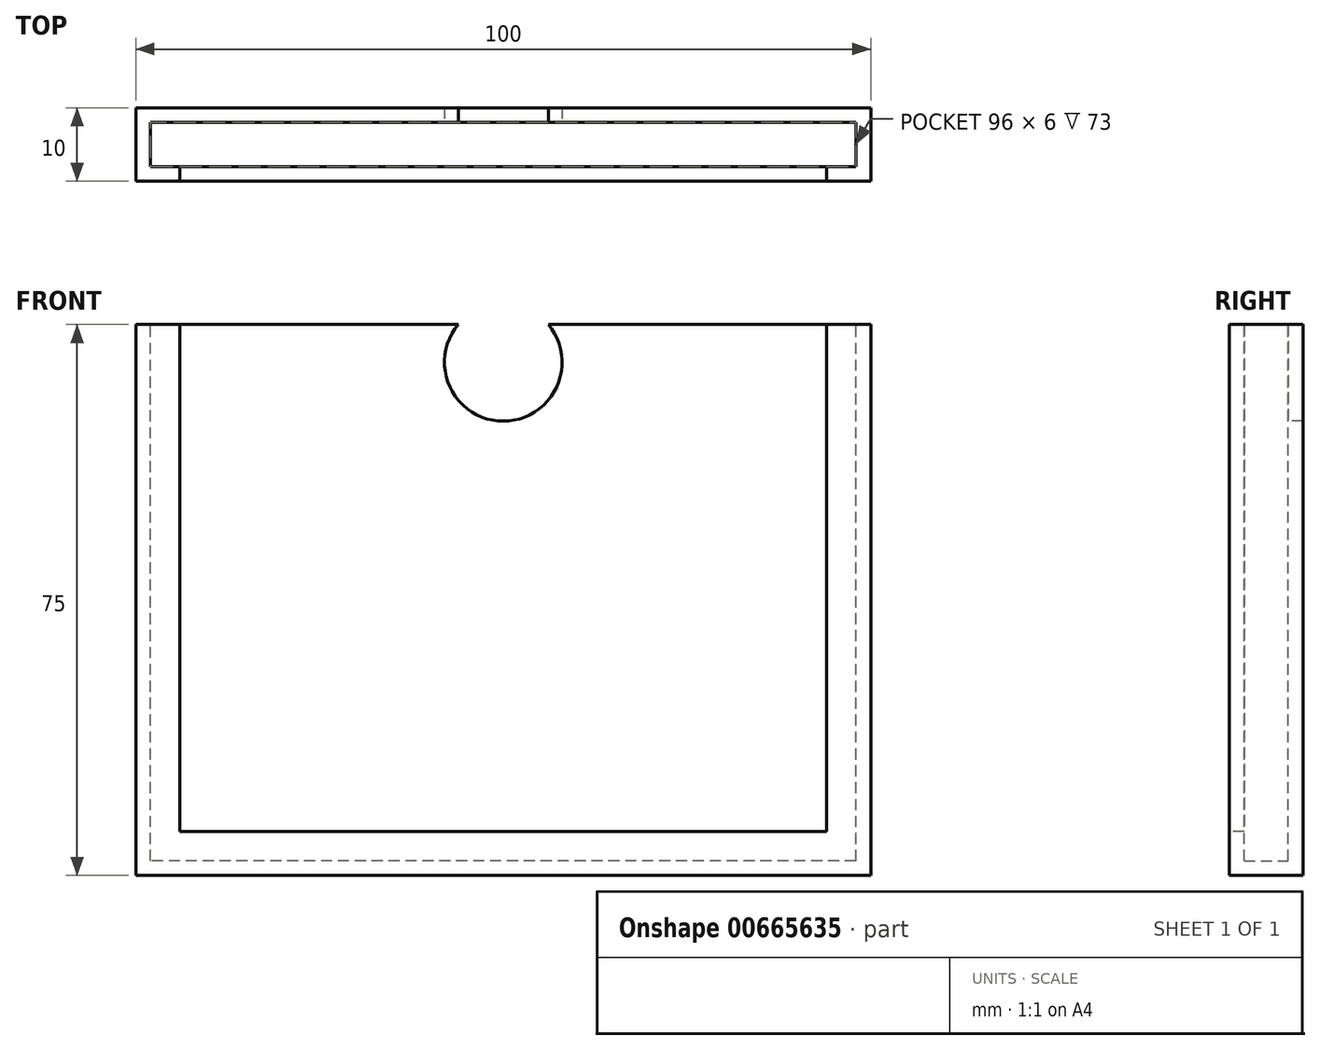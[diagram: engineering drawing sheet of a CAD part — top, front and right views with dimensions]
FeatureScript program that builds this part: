
annotation { "Feature Type Name" : "Feature", "Feature Type Description" : "" }
export const myFeature = defineFeature(function(context is Context, id is Id, definition is map)
    precondition{}
    {
        {
            var Q0;
            Q0=qCreatedBy(makeId("Front.planeOp"),FACE);
            var sketch = newSketch(context, id + "F0", { "sketchPlane" : qUnion([Q0])});
            skLineSegment(sketch, "E0.bottom", {"start": v(0, 0) * mm, "end": v(-100, 0) * mm});
            skLineSegment(sketch, "E0.top", {"start": v(0, 75) * mm, "end": v(-100, 75) * mm});
            skLineSegment(sketch, "E0.left", {"start": v(0, 0) * mm, "end": v(0, 75) * mm});
            skLineSegment(sketch, "E0.right", {"start": v(-100, 0) * mm, "end": v(-100, 75) * mm});
            skSolve(sketch);
        }
        {
            var Q0;
            Q0 = qSketchRegion(id + "F0", true);
            var Q1;
            Q1=makeQuery(id+"F0.imprint","IMPRINT",FACE,{"disambiguationData":[TD([[makeQuery(id+"F0.imprint","IMPRINT",EDGE,{"derivedFrom":sQuery(id+"F0.wireOp",EDGE,"E0.bottom")}),-1.0]])]});
            extrude(context, id + "F1", {"entities" : qUnion([Q0, Q1]), "depth" : 10 * mm, "offsetDistance" : 25 * mm});
        }
        {
            var Q0;
            Q0=makeQuery(id+"F1.opExtrude","SWEPT_FACE",FACE,{"disambiguationData":[OSD([sQuery(id+"F0.wireOp",EDGE,"E0.top")])]});
            shell(context, id + "F2", {"entities" : qUnion([Q0]), "thickness" : 2 * mm});
        }
        {
            var Q0;
            Q0=makeQuery(id+"F1.opExtrude","CAP_FACE",FACE,{"disambiguationData":[OSD([sQuery(id+"F0.wireOp",EDGE,"E0.bottom"),sQuery(id+"F0.wireOp",EDGE,"E0.top"),sQuery(id+"F0.wireOp",EDGE,"E0.left"),sQuery(id+"F0.wireOp",EDGE,"E0.right")])],"isStart":false});
            var sketch = newSketch(context, id + "F3", { "sketchPlane" : qUnion([Q0])});
            skLineSegment(sketch, "E1.bottom", {"start": v(-94, 75) * mm, "end": v(-6, 75) * mm});
            skLineSegment(sketch, "E1.top", {"start": v(-94, 6) * mm, "end": v(-6, 6) * mm});
            skLineSegment(sketch, "E1.left", {"start": v(-94, 75) * mm, "end": v(-94, 6) * mm});
            skLineSegment(sketch, "E1.right", {"start": v(-6, 75) * mm, "end": v(-6, 6) * mm});
            skSolve(sketch);
        }
        {
            var Q0;
            Q0=makeQuery(id+"F3.imprint","IMPRINT",FACE,{"disambiguationData":[TD([[makeQuery(id+"F3.imprint","IMPRINT",EDGE,{"derivedFrom":sQuery(id+"F3.wireOp",EDGE,"E1.bottom")}),1.0]])]});
            extrude(context, id + "F4", {"entities" : qUnion([Q0]), "operationType" : NewBodyOperationType.REMOVE, "oppositeDirection" : true, "depth" : 5 * mm, "offsetDistance" : 25 * mm});
        }
        {
            var Q0;
            Q0=makeQuery(id+"F3.imprint","IMPRINT",FACE,{"disambiguationData":[TD([[makeQuery(id+"F3.imprint","IMPRINT",EDGE,{"derivedFrom":sQuery(id+"F3.wireOp",EDGE,"E1.bottom")}),1.0]])]});
            var sketch = newSketch(context, id + "F5", { "sketchPlane" : qUnion([Q0])});
            skCircle(sketch, "E2", {"center": v(-50, 69.84) * mm, "radius": 8 * mm});
            skSolve(sketch);
        }
        {
            var Q0;
            {var subQ0=sQuery(id+"F5.wireOp",EDGE,"E2");var subQ1=makeQuery(id+"F3.imprint","IMPRINT",EDGE,{"derivedFrom":sQuery(id+"F3.wireOp",EDGE,"E1.bottom")});var subQ2=makeQuery(id+"F5.imprint","INTERSECT",VERTEX,{"disambiguationData":[OD(0.0)],"derivedFrom":[subQ1,subQ0]});Q0=makeQuery(id+"F5.imprint","IMPRINT",FACE,{"disambiguationData":[TD([[makeQuery(id+"F5.imprint","IMPRINT",EDGE,{"disambiguationData":[TD([[subQ2,1.0]])],"derivedFrom":subQ0}),1.0]])]});}
            extrude(context, id + "F6", {"entities" : qUnion([Q0]), "operationType" : NewBodyOperationType.REMOVE, "endBound" : BoundingType.THROUGH_ALL, "oppositeDirection" : true, "depth" : 25 * mm, "offsetDistance" : 25 * mm});
        }
    });
